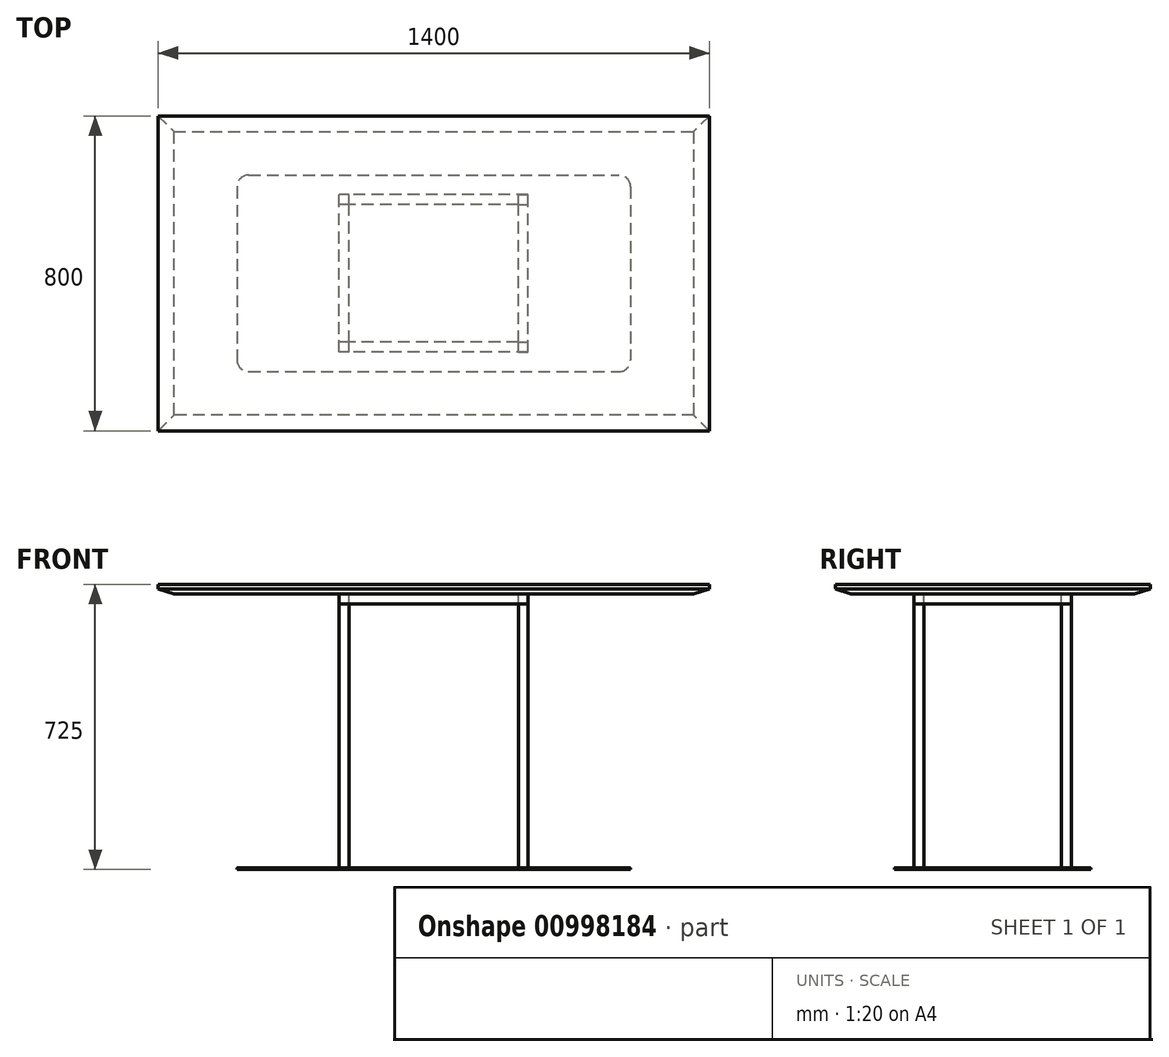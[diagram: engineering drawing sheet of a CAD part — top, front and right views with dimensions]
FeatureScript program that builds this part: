
annotation { "Feature Type Name" : "Feature", "Feature Type Description" : "" }
export const myFeature = defineFeature(function(context is Context, id is Id, definition is map)
    precondition{}
    {
        {
            var Q0;
            Q0=qCreatedBy(makeId("Top.planeOp"),FACE);
            cPlane(context, id + "F0", {"entities" : qUnion([Q0]), "cplaneType" : CPlaneType.OFFSET, "offset" : 700 * mm, "width" : 150 * mm, "height" : 150 * mm});
        }
        {
            var Q0;
            Q0=qCreatedBy(id+"F0.planeOp",FACE);
            var sketch = newSketch(context, id + "F1", { "sketchPlane" : qUnion([Q0])});
            skLineSegment(sketch, "E0.bottom", {"start": v(0, 0) * mm, "end": v(-1400, 0) * mm});
            skLineSegment(sketch, "E0.top", {"start": v(0, 800) * mm, "end": v(-1400, 800) * mm});
            skLineSegment(sketch, "E0.left", {"start": v(0, 0) * mm, "end": v(0, 800) * mm});
            skLineSegment(sketch, "E0.right", {"start": v(-1400, 0) * mm, "end": v(-1400, 800) * mm});
            skSolve(sketch);
        }
        {
            var Q0;
            Q0 = qSketchRegion(id + "F1", true);
            extrude(context, id + "F2", {"entities" : qUnion([Q0]), "depth" : 25 * mm, "offsetDistance" : 25 * mm});
        }
        {
            var Q0;
            Q0=makeQuery(id+"F2.opExtrude","CAP_FACE",FACE,{"disambiguationData":[OSD([sQuery(id+"F1.wireOp",EDGE,"E0.bottom"),sQuery(id+"F1.wireOp",EDGE,"E0.top"),sQuery(id+"F1.wireOp",EDGE,"E0.left"),sQuery(id+"F1.wireOp",EDGE,"E0.right")])],"isStart":true});
            chamfer(context, id + "F3", {"entities" : qUnion([Q0]), "chamferType" : ChamferType.TWO_OFFSETS, "width1" : 40 * mm, "oppositeDirection" : false, "width2" : 12.5 * mm, "tangentPropagation" : true});
        }
        {
            var Q0;
            Q0=makeQuery(id+"F2.opExtrude","CAP_FACE",FACE,{"disambiguationData":[OSD([sQuery(id+"F1.wireOp",EDGE,"E0.bottom"),sQuery(id+"F1.wireOp",EDGE,"E0.top"),sQuery(id+"F1.wireOp",EDGE,"E0.left"),sQuery(id+"F1.wireOp",EDGE,"E0.right")])],"isStart":true});
            cPlane(context, id + "F4", {"entities" : qUnion([Q0]), "cplaneType" : CPlaneType.OFFSET, "offset" : 0 * mm, "width" : 150 * mm, "height" : 150 * mm});
        }
        {
            var Q0;
            Q0=qCreatedBy(id+"F4.planeOp",FACE);
            var sketch = newSketch(context, id + "F5", { "sketchPlane" : qUnion([Q0])});
            skLineSegment(sketch, "E1", {"start": v(0, 0) * mm, "end": v(-460, 0) * mm, "construction": true});
            skLineSegment(sketch, "E2", {"start": v(-460, 0) * mm, "end": v(-460, -200) * mm, "construction": true});
            skLineSegment(sketch, "E3.bottom", {"start": v(0, 0) * mm, "end": v(-1400, 0) * mm, "construction": true});
            skLineSegment(sketch, "E3.top", {"start": v(0, -800) * mm, "end": v(-1400, -800) * mm, "construction": true});
            skLineSegment(sketch, "E3.left", {"start": v(0, 0) * mm, "end": v(0, -800) * mm, "construction": true});
            skLineSegment(sketch, "E3.right", {"start": v(-1400, 0) * mm, "end": v(-1400, -800) * mm, "construction": true});
            skLineSegment(sketch, "E4", {"start": v(-1400, 0) * mm, "end": v(-940, 0) * mm, "construction": true});
            skLineSegment(sketch, "E5", {"start": v(-940, -800) * mm, "end": v(-940, -600) * mm, "construction": true});
            skLineSegment(sketch, "E6.bottom", {"start": v(-460, -200) * mm, "end": v(-940, -200) * mm});
            skLineSegment(sketch, "E6.top", {"start": v(-460, -600) * mm, "end": v(-940, -600) * mm});
            skLineSegment(sketch, "E6.left", {"start": v(-460, -200) * mm, "end": v(-460, -600) * mm});
            skLineSegment(sketch, "E6.right", {"start": v(-940, -200) * mm, "end": v(-940, -600) * mm});
            skLineSegment(sketch, "E7.0", {"start": v(-485, -225) * mm, "end": v(-915, -225) * mm});
            skLineSegment(sketch, "E8.0", {"start": v(-915, -225) * mm, "end": v(-915, -575) * mm});
            skLineSegment(sketch, "E9.0", {"start": v(-485, -575) * mm, "end": v(-915, -575) * mm});
            skLineSegment(sketch, "E10.0", {"start": v(-485, -225) * mm, "end": v(-485, -575) * mm});
            skSolve(sketch);
        }
        {
            var Q0;
            Q0 = qSketchRegion(id + "F5", true);
            extrude(context, id + "F6", {"entities" : qUnion([Q0]), "operationType" : NewBodyOperationType.ADD, "depth" : 25 * mm, "offsetDistance" : 25 * mm});
        }
        {
            var Q0;
            Q0=makeQuery(id+"F6.opExtrude","SWEPT_FACE",FACE,{"disambiguationData":[OSD([sQuery(id+"F5.wireOp",EDGE,"E6.left")])]});
            cPlane(context, id + "F7", {"entities" : qUnion([Q0]), "cplaneType" : CPlaneType.OFFSET, "offset" : 0 * mm, "width" : 150 * mm, "height" : 150 * mm});
        }
        {
            var Q0;
            Q0=qCreatedBy(id+"F7.planeOp",FACE);
            var sketch = newSketch(context, id + "F8", { "sketchPlane" : qUnion([Q0])});
            skLineSegment(sketch, "E11", {"start": v(200, 0) * mm, "end": v(200, 675) * mm, "construction": true});
            skLineSegment(sketch, "E12.bottom", {"start": v(200, 675) * mm, "end": v(225, 675) * mm});
            skLineSegment(sketch, "E12.top", {"start": v(200, 0) * mm, "end": v(600, 0) * mm});
            skLineSegment(sketch, "E12.left", {"start": v(200, 675) * mm, "end": v(200, 0) * mm});
            skLineSegment(sketch, "E12.right", {"start": v(600, 675) * mm, "end": v(600, 0) * mm});
            skLineSegment(sketch, "E13", {"start": v(200, 675) * mm, "end": v(225, 675) * mm, "construction": true});
            skLineSegment(sketch, "E14.left", {"start": v(225, 650) * mm, "end": v(225, 25) * mm});
            skLineSegment(sketch, "E14.right", {"start": v(575, 650) * mm, "end": v(575, 25) * mm});
            skLineSegment(sketch, "E15", {"start": v(225, 650) * mm, "end": v(225, 675) * mm});
            skLineSegment(sketch, "E16", {"start": v(575, 650) * mm, "end": v(575, 675) * mm});
            skLineSegment(sketch, "E17.trimOffspring", {"start": v(575, 675) * mm, "end": v(600, 675) * mm});
            skLineSegment(sketch, "E18", {"start": v(225, 25) * mm, "end": v(225, 30) * mm, "construction": true});
            skLineSegment(sketch, "E19", {"start": v(225, 25) * mm, "end": v(225, 0) * mm});
            skLineSegment(sketch, "E20", {"start": v(575, 25) * mm, "end": v(575, 0) * mm});
            skSolve(sketch);
        }
        {
            var Q0;
            Q0 = qSketchRegion(id + "F8", true);
            extrude(context, id + "F9", {"entities" : qUnion([Q0]), "oppositeDirection" : true, "depth" : 25 * mm, "offsetDistance" : 25 * mm});
        }
        {
            var Q0;
            Q0=makeQuery(id+"F6.opExtrude","SWEPT_FACE",FACE,{"disambiguationData":[OSD([sQuery(id+"F5.wireOp",EDGE,"E6.right")])]});
            cPlane(context, id + "F10", {"entities" : qUnion([Q0]), "cplaneType" : CPlaneType.OFFSET, "offset" : 0 * mm, "width" : 150 * mm, "height" : 150 * mm});
        }
        {
            var Q0;
            Q0=qCreatedBy(id+"F10.planeOp",FACE);
            var sketch = newSketch(context, id + "F11", { "sketchPlane" : qUnion([Q0])});
            skLineSegment(sketch, "E21", {"start": v(0, 0) * mm, "end": v(-200, 0) * mm, "construction": true});
            skLineSegment(sketch, "E22.bottom", {"start": v(-200, 0) * mm, "end": v(-600, 0) * mm});
            skLineSegment(sketch, "E22.top", {"start": v(-200, 675) * mm, "end": v(-225, 675) * mm});
            skLineSegment(sketch, "E22.left", {"start": v(-200, 0) * mm, "end": v(-200, 675) * mm});
            skLineSegment(sketch, "E22.right", {"start": v(-600, 0) * mm, "end": v(-600, 675) * mm});
            skLineSegment(sketch, "E23", {"start": v(-600, 675) * mm, "end": v(-575, 675) * mm, "construction": true});
            skLineSegment(sketch, "E24.left", {"start": v(-575, 675) * mm, "end": v(-575, 25) * mm});
            skLineSegment(sketch, "E24.right", {"start": v(-225, 675) * mm, "end": v(-225, 25) * mm});
            skLineSegment(sketch, "E25.trimOffspring", {"start": v(-575, 675) * mm, "end": v(-600, 675) * mm});
            skLineSegment(sketch, "E26", {"start": v(-575, 25) * mm, "end": v(-575, 30) * mm, "construction": true});
            skLineSegment(sketch, "E27", {"start": v(-575, 25) * mm, "end": v(-575, 0) * mm});
            skLineSegment(sketch, "E28", {"start": v(-225, 25) * mm, "end": v(-225, 0) * mm});
            skPoint(sketch, "E29.end.orphan", {"position": v(-225, 30) * mm});
            skSolve(sketch);
        }
        {
            var Q0;
            Q0 = qSketchRegion(id + "F11", true);
            extrude(context, id + "F12", {"entities" : qUnion([Q0]), "oppositeDirection" : true, "depth" : 25 * mm, "offsetDistance" : 25 * mm});
        }
        {
            var Q0;
            {var subQ0=sQuery(id+"F8.wireOp",EDGE,"E12.top");Q0=makeQuery(id+"F9.opExtrude","SWEPT_FACE",FACE,{"disambiguationData":[OSD([subQ0]),TDD([makeQuery(id+"F8.imprint","IMPRINT",EDGE,{"disambiguationData":[TD([[makeQuery(id+"F8.imprint","INTERSECT",VERTEX,{"derivedFrom":[subQ0,sQuery(id+"F8.wireOp",EDGE,"E12.right")]}),1.0]])],"derivedFrom":subQ0})])]});}
            cPlane(context, id + "F13", {"entities" : qUnion([Q0]), "cplaneType" : CPlaneType.OFFSET, "offset" : 0 * mm, "width" : 150 * mm, "height" : 150 * mm});
        }
        {
            var Q0;
            Q0=qCreatedBy(id+"F13.planeOp",FACE);
            var sketch = newSketch(context, id + "F14", { "sketchPlane" : qUnion([Q0])});
            skLineSegment(sketch, "E30", {"start": v(0, 0) * mm, "end": v(-200, 0) * mm, "construction": true});
            skLineSegment(sketch, "E31", {"start": v(-200, 0) * mm, "end": v(-200, -150) * mm, "construction": true});
            skLineSegment(sketch, "E32", {"start": v(0, 0) * mm, "end": v(0, -800) * mm, "construction": true});
            skLineSegment(sketch, "E33", {"start": v(0, -800) * mm, "end": v(-1200, -800) * mm, "construction": true});
            skLineSegment(sketch, "E34", {"start": v(-1200, -800) * mm, "end": v(-1200, -650) * mm, "construction": true});
            skLineSegment(sketch, "E35.bottom", {"start": v(-1200, -650) * mm, "end": v(-200, -650) * mm});
            skLineSegment(sketch, "E35.top", {"start": v(-1200, -150) * mm, "end": v(-200, -150) * mm});
            skLineSegment(sketch, "E35.left", {"start": v(-1200, -650) * mm, "end": v(-1200, -150) * mm});
            skLineSegment(sketch, "E35.right", {"start": v(-200, -650) * mm, "end": v(-200, -150) * mm});
            skSolve(sketch);
        }
        {
            var Q0;
            Q0 = qSketchRegion(id + "F14", true);
            extrude(context, id + "F15", {"entities" : qUnion([Q0]), "oppositeDirection" : true, "depth" : 5 * mm, "offsetDistance" : 25 * mm});
        }
        {
            var Q0;
            Q0=makeQuery(id+"F15.opExtrude","SWEPT_EDGE",EDGE,{"disambiguationData":[OSD([sQuery(id+"F14.wireOp",EDGE,"E35.top"),sQuery(id+"F14.wireOp",EDGE,"E35.left")])]});
            var Q1;
            Q1=makeQuery(id+"F15.opExtrude","SWEPT_EDGE",EDGE,{"disambiguationData":[OSD([sQuery(id+"F14.wireOp",EDGE,"E35.bottom"),sQuery(id+"F14.wireOp",EDGE,"E35.left")])]});
            var Q2;
            Q2=makeQuery(id+"F15.opExtrude","SWEPT_EDGE",EDGE,{"disambiguationData":[OSD([sQuery(id+"F14.wireOp",EDGE,"E35.bottom"),sQuery(id+"F14.wireOp",EDGE,"E35.right")])]});
            var Q3;
            Q3=makeQuery(id+"F15.opExtrude","SWEPT_EDGE",EDGE,{"disambiguationData":[OSD([sQuery(id+"F14.wireOp",EDGE,"E35.top"),sQuery(id+"F14.wireOp",EDGE,"E35.right")])]});
            fillet(context, id + "F16", {"entities" : qUnion([Q0, Q1, Q2, Q3]), "radius" : 30 * mm, "tangentPropagation" : true, "allowEdgeOverflow" : false});
        }
        {
            var Q0;
            Q0=makeQuery(id+"F15.opExtrude","CAP_EDGE",EDGE,{"disambiguationData":[OSD([sQuery(id+"F14.wireOp",EDGE,"E35.right")])],"isStart":false});
            var Q1;
            {var subQ0=sQuery(id+"F14.wireOp",EDGE,"E35.right");var subQ1=sQuery(id+"F14.wireOp",EDGE,"E35.bottom");Q1=makeQuery(id+"F16.opFillet","BLEND_EDGE",EDGE,{"blendedFrom":[makeQuery(id+"F15.opExtrude","SWEPT_EDGE",EDGE,{"disambiguationData":[OSD([subQ1,subQ0])]}),makeQuery(id+"F15.opExtrude","CAP_FACE",FACE,{"disambiguationData":[OSD([subQ1,sQuery(id+"F14.wireOp",EDGE,"E35.top"),sQuery(id+"F14.wireOp",EDGE,"E35.left"),subQ0])],"isStart":false})],"blendedInto":[makeQuery(id+"F15.opExtrude","CAP_FACE",FACE,{"disambiguationData":[OSD([subQ1,sQuery(id+"F14.wireOp",EDGE,"E35.top"),sQuery(id+"F14.wireOp",EDGE,"E35.left"),subQ0])],"isStart":false})]});}
            var Q2;
            Q2=makeQuery(id+"F15.opExtrude","CAP_EDGE",EDGE,{"disambiguationData":[OSD([sQuery(id+"F14.wireOp",EDGE,"E35.bottom")])],"isStart":false});
            var Q3;
            {var subQ0=sQuery(id+"F14.wireOp",EDGE,"E35.left");var subQ1=sQuery(id+"F14.wireOp",EDGE,"E35.bottom");Q3=makeQuery(id+"F16.opFillet","BLEND_EDGE",EDGE,{"blendedFrom":[makeQuery(id+"F15.opExtrude","SWEPT_EDGE",EDGE,{"disambiguationData":[OSD([subQ1,subQ0])]}),makeQuery(id+"F15.opExtrude","CAP_FACE",FACE,{"disambiguationData":[OSD([subQ1,sQuery(id+"F14.wireOp",EDGE,"E35.top"),subQ0,sQuery(id+"F14.wireOp",EDGE,"E35.right")])],"isStart":false})],"blendedInto":[makeQuery(id+"F15.opExtrude","CAP_FACE",FACE,{"disambiguationData":[OSD([subQ1,sQuery(id+"F14.wireOp",EDGE,"E35.top"),subQ0,sQuery(id+"F14.wireOp",EDGE,"E35.right")])],"isStart":false})]});}
            var Q4;
            Q4=makeQuery(id+"F15.opExtrude","CAP_EDGE",EDGE,{"disambiguationData":[OSD([sQuery(id+"F14.wireOp",EDGE,"E35.left")])],"isStart":false});
            var Q5;
            Q5=makeQuery(id+"F15.opExtrude","CAP_EDGE",EDGE,{"disambiguationData":[OSD([sQuery(id+"F14.wireOp",EDGE,"E35.top")])],"isStart":false});
            var Q6;
            {var subQ0=sQuery(id+"F14.wireOp",EDGE,"E35.right");var subQ1=sQuery(id+"F14.wireOp",EDGE,"E35.top");Q6=makeQuery(id+"F16.opFillet","BLEND_EDGE",EDGE,{"blendedFrom":[makeQuery(id+"F15.opExtrude","SWEPT_EDGE",EDGE,{"disambiguationData":[OSD([subQ1,subQ0])]}),makeQuery(id+"F15.opExtrude","CAP_FACE",FACE,{"disambiguationData":[OSD([sQuery(id+"F14.wireOp",EDGE,"E35.bottom"),subQ1,sQuery(id+"F14.wireOp",EDGE,"E35.left"),subQ0])],"isStart":false})],"blendedInto":[makeQuery(id+"F15.opExtrude","CAP_FACE",FACE,{"disambiguationData":[OSD([sQuery(id+"F14.wireOp",EDGE,"E35.bottom"),subQ1,sQuery(id+"F14.wireOp",EDGE,"E35.left"),subQ0])],"isStart":false})]});}
            var Q7;
            {var subQ0=sQuery(id+"F14.wireOp",EDGE,"E35.left");var subQ1=sQuery(id+"F14.wireOp",EDGE,"E35.top");Q7=makeQuery(id+"F16.opFillet","BLEND_EDGE",EDGE,{"blendedFrom":[makeQuery(id+"F15.opExtrude","SWEPT_EDGE",EDGE,{"disambiguationData":[OSD([subQ1,subQ0])]}),makeQuery(id+"F15.opExtrude","CAP_FACE",FACE,{"disambiguationData":[OSD([sQuery(id+"F14.wireOp",EDGE,"E35.bottom"),subQ1,subQ0,sQuery(id+"F14.wireOp",EDGE,"E35.right")])],"isStart":false})],"blendedInto":[makeQuery(id+"F15.opExtrude","CAP_FACE",FACE,{"disambiguationData":[OSD([sQuery(id+"F14.wireOp",EDGE,"E35.bottom"),subQ1,subQ0,sQuery(id+"F14.wireOp",EDGE,"E35.right")])],"isStart":false})]});}
            fillet(context, id + "F17", {"entities" : qUnion([Q0, Q1, Q2, Q3, Q4, Q5, Q6, Q7]), "radius" : 3 * mm, "tangentPropagation" : true, "allowEdgeOverflow" : false});
        }
    });
